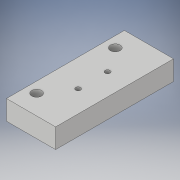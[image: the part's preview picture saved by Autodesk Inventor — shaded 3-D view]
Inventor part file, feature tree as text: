
AUTODESK INVENTOR PART (.ipt)
format: ipt  version: 2017 (Build 210142000, 142)  size: 105,984 bytes
history: native  units: in
note: dims shown in document units (in); Inventor stores cm internally (conversion verified against a paired STEP export)
features: extrude x1, sketch x1
ambient origin geometry x8: Origin, YZ Plane, XZ Plane, XY Plane, X Axis, Y Axis, Z Axis, Center Point
bodies: Solid1 (feature_tree)
feature tree (2):
  extrude  "Extrusion1"  Depth=1.5in
  sketch  "Sketch1"  dims[d0=0.625in d1=1.5in d2=0.303in d3=0.188in d4=0.5in d5=0.125in d7=0.1875in d8=0.063in d9=0.25in d10=0.0in d11=0.276in]
